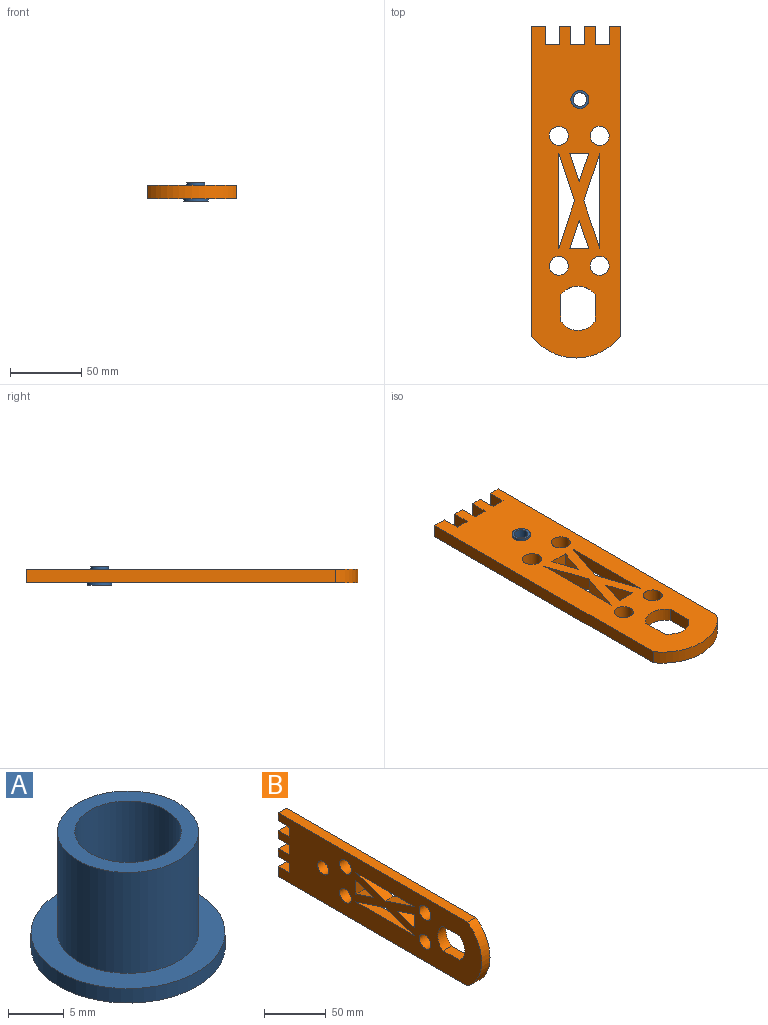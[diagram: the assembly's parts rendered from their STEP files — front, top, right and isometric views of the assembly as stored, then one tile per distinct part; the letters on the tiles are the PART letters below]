
ASSEMBLY  parts=2 mates=1
PART A: 6 faces, bbox 17.5x17.5x12.7 mm
  f0: plane 12.7x12.7mm, normal (0,0,1), area 54.7mm2, adj f2,f3
  f1: plane 17.46x17.46mm, normal (0,0,-1), area 167.5mm2, adj f3,f5
  f2: cylinder r=6.35mm len=12.7mm, axis (0,0,-1), area 443.4mm2, adj f0,f4
  f3: cylinder r=4.79mm len=12.7mm, axis (0,0,-1), area 382.1mm2, adj f0,f1
  f4: plane 17.46x17.46mm, normal (0,0,1), area 112.8mm2, adj f2,f5
  f5: cylinder r=8.73mm len=17.46mm, axis (0,0,-1), area 87.1mm2, adj f1,f4
PART B: 39 faces, bbox 9.5x233.7x63.3 mm
  f0: plane 217.57x9.53mm, normal (0,0,-1), area 2072.3mm2, adj f2,f3,f34,f38
  f1: plane 217.57x9.53mm, normal (0,0,1), area 2072.3mm2, adj f2,f3,f37,f38
  f2: plane 233.72x63.28mm, normal (-1,0,0), area 11736.7mm2, adj f0,f1,f4,f5,f6,f7,f8,f9
  f3: plane 233.72x63.28mm, normal (1,0,0), area 11736.7mm2, adj f0,f1,f4,f5,f6,f7,f8,f9
  f4: plane 9.87x9.53mm, normal (0,1,0), area 94mm2, adj f2,f3,f30,f32
  f5: plane 9.87x9.53mm, normal (0,1,0), area 94mm2, adj f2,f3,f31,f33
  f6: plane 9.87x9.53mm, normal (0,1,0), area 94mm2, adj f2,f3,f28,f29
  f7: cylinder r=14.98mm len=24.17mm, axis (-1,0,0), area 267.8mm2, adj f2,f3,f8,f10
  f8: plane 18.4x9.53mm, normal (0,0,-1), area 175.3mm2, adj f2,f3,f7,f9
  f9: cylinder r=14.33mm len=24.17mm, axis (-1,0,0), area 273.9mm2, adj f2,f3,f8,f10
  f10: plane 18.4x9.53mm, normal (0,0,1), area 175.3mm2, adj f2,f3,f7,f9
  f11: plane 33.67x11.18mm, normal (0,0.32,0.95), area 337.9mm2, adj f2,f3,f12,f23
  f12: plane 33.67x11.18mm, normal (0,-0.32,0.95), area 337.9mm2, adj f2,f3,f11,f23
  f13: plane 20.15x9.53mm, normal (0,0.32,0.95), area 202.2mm2, adj f2,f3,f14,f24
  f14: plane 20.15x9.53mm, normal (0,0.32,-0.95), area 202.2mm2, adj f2,f3,f13,f24
  f15: cylinder r=6.69mm len=13.38mm, axis (1,0,0), area 400.4mm2, adj f2,f3
  f16: plane 20.15x9.53mm, normal (0,-0.32,0.95), area 202.2mm2, adj f2,f3,f17,f26
  f17: plane 20.15x9.53mm, normal (0,-0.32,-0.95), area 202.2mm2, adj f2,f3,f16,f26
  f18: plane 33.67x11.18mm, normal (0,-0.32,-0.95), area 337.9mm2, adj f2,f3,f19,f25
  f19: plane 33.67x11.18mm, normal (0,0.32,-0.95), area 337.9mm2, adj f2,f3,f18,f25
  f20: cylinder r=6.69mm len=13.38mm, axis (1,0,0), area 400.4mm2, adj f2,f3
  f21: cylinder r=6.69mm len=13.38mm, axis (1,0,0), area 400.4mm2, adj f2,f3
  f22: cylinder r=6.69mm len=13.38mm, axis (1,0,0), area 400.4mm2, adj f2,f3
  f23: plane 67.33x9.53mm, normal (0,0,-1), area 641.4mm2, adj f2,f3,f11,f12
  f24: plane 13.39x9.53mm, normal (0,-1,0), area 127.5mm2, adj f2,f3,f13,f14
  f25: plane 67.33x9.53mm, normal (0,0,1), area 641.4mm2, adj f2,f3,f18,f19
  f26: plane 13.39x9.53mm, normal (0,1,0), area 127.5mm2, adj f2,f3,f16,f17
  f27: cylinder r=6.29mm len=12.57mm, axis (1,0,0), area 376.2mm2, adj f2,f3
  f28: plane 12.7x9.53mm, normal (0,0,-1), area 121mm2, adj f2,f3,f6,f37
  f29: plane 12.7x9.53mm, normal (0,0,1), area 121mm2, adj f2,f3,f6,f36
  f30: plane 12.7x9.53mm, normal (0,0,-1), area 121mm2, adj f2,f3,f4,f36
  f31: plane 12.7x9.53mm, normal (0,0,1), area 121mm2, adj f2,f3,f5,f34
  f32: plane 12.7x9.53mm, normal (0,0,1), area 121mm2, adj f2,f3,f4,f35
  f33: plane 12.7x9.53mm, normal (0,0,-1), area 121mm2, adj f2,f3,f5,f35
  f34: plane 9.94x9.53mm, normal (0,1,0), area 94.7mm2, adj f0,f2,f3,f31
  f35: plane 9.53x7.91mm, normal (0,1,0), area 75.3mm2, adj f2,f3,f32,f33
  f36: plane 9.53x7.91mm, normal (0,1,0), area 75.3mm2, adj f2,f3,f29,f30
  f37: plane 9.53x7.91mm, normal (0,1,0), area 75.3mm2, adj f1,f2,f3,f28
  f38: cylinder r=39.06mm len=63.28mm, axis (1,0,0), area 702.5mm2, adj f0,f1,f2,f3
PLACE A t=(59.97,32.69,-19.29)mm
PLACE B rot(axis=(0,1,0),90deg) t=(64.75,-51.79,-8.18)mm
MATE fastened B.f27 <-> A.f2  axis (0,0,-1) through (59.97,32.69,-17.7)mm
